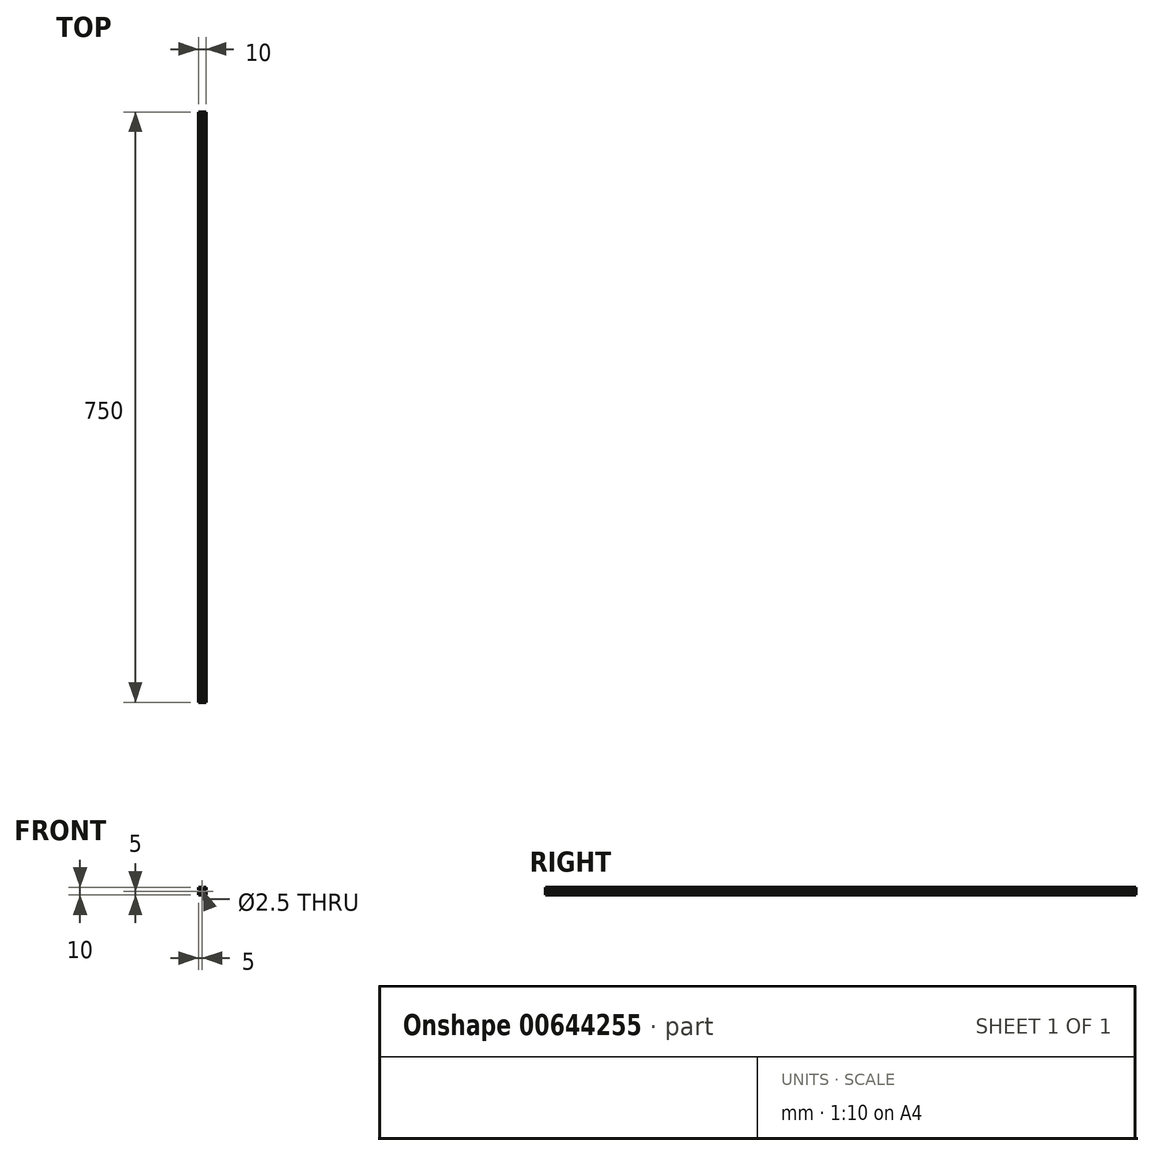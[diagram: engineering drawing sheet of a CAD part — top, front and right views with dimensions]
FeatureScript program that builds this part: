
annotation { "Feature Type Name" : "Feature", "Feature Type Description" : "" }
export const myFeature = defineFeature(function(context is Context, id is Id, definition is map)
    precondition{}
    {
        {
            var Q0;
            Q0=qCreatedBy(makeId("Front.planeOp"),FACE);
            var sketch = newSketch(context, id + "F0", { "sketchPlane" : qUnion([Q0])});
            skCircle(sketch, "E0", {"center": v(0, 0) * mm, "radius": 1.25 * mm});
            skLineSegment(sketch, "E1", {"start": v(1.5, 5) * mm, "end": v(5, 5) * mm});
            skLineSegment(sketch, "E2", {"start": v(5, 5) * mm, "end": v(5, 1.5) * mm});
            skLineSegment(sketch, "E3", {"start": v(5, -5) * mm, "end": v(1.5, -5) * mm});
            skLineSegment(sketch, "E4", {"start": v(-1.5, 5) * mm, "end": v(-5, 5) * mm});
            skLineSegment(sketch, "E5", {"start": v(-5, -5) * mm, "end": v(-5, -1.5) * mm});
            skLineSegment(sketch, "E6", {"start": v(5, -5) * mm, "end": v(5, -1.5) * mm});
            skLineSegment(sketch, "E7", {"start": v(5, -1.5) * mm, "end": v(4, -1.5) * mm});
            skLineSegment(sketch, "E8", {"start": v(1.5, -5) * mm, "end": v(1.5, -4) * mm});
            skLineSegment(sketch, "E9", {"start": v(0, 2) * mm, "end": v(-1, 2) * mm});
            skLineSegment(sketch, "E10", {"start": v(0, 2) * mm, "end": v(1, 2) * mm});
            skLineSegment(sketch, "E11", {"start": v(0, -2) * mm, "end": v(1, -2) * mm});
            skLineSegment(sketch, "E12", {"start": v(1.5, -4) * mm, "end": v(3, -4) * mm});
            skLineSegment(sketch, "E13", {"start": v(0, -2) * mm, "end": v(-1, -2) * mm});
            skLineSegment(sketch, "E14", {"start": v(4, -1.5) * mm, "end": v(4, -3) * mm});
            skLineSegment(sketch, "E15", {"start": v(0, 0) * mm, "end": v(1.25, 0) * mm});
            skLineSegment(sketch, "E16", {"start": v(-2, 0) * mm, "end": v(-2, 1) * mm});
            skLineSegment(sketch, "E17", {"start": v(-2, 0) * mm, "end": v(-2, -1) * mm});
            skLineSegment(sketch, "E18", {"start": v(2, 0) * mm, "end": v(2, 1) * mm});
            skLineSegment(sketch, "E19", {"start": v(2, 0) * mm, "end": v(2, -1) * mm});
            skLineSegment(sketch, "E20", {"start": v(1, -2) * mm, "end": v(3, -4) * mm});
            skLineSegment(sketch, "E21", {"start": v(2, -1) * mm, "end": v(4, -3) * mm});
            skLineSegment(sketch, "E22", {"start": v(5, 5) * mm, "end": v(1.5, 5) * mm});
            skLineSegment(sketch, "E23", {"start": v(1.5, 5) * mm, "end": v(1.5, 4) * mm});
            skLineSegment(sketch, "E24", {"start": v(5, 1.5) * mm, "end": v(4, 1.5) * mm});
            skLineSegment(sketch, "E25", {"start": v(4, 1.5) * mm, "end": v(4, 3) * mm});
            skLineSegment(sketch, "E26", {"start": v(1.5, 4) * mm, "end": v(3, 4) * mm});
            skLineSegment(sketch, "E27", {"start": v(1, 2) * mm, "end": v(3, 4) * mm});
            skLineSegment(sketch, "E28", {"start": v(2, 1) * mm, "end": v(4, 3) * mm});
            skLineSegment(sketch, "E29", {"start": v(-5, -5) * mm, "end": v(-1.5, -5) * mm});
            skLineSegment(sketch, "E30", {"start": v(-5, -1.5) * mm, "end": v(-4, -1.5) * mm});
            skLineSegment(sketch, "E31", {"start": v(-1.5, -5) * mm, "end": v(-1.5, -4) * mm});
            skLineSegment(sketch, "E32", {"start": v(-1.5, -4) * mm, "end": v(-3, -4) * mm});
            skLineSegment(sketch, "E33", {"start": v(-4, -1.5) * mm, "end": v(-4, -3) * mm});
            skLineSegment(sketch, "E34", {"start": v(-1, -2) * mm, "end": v(-3, -4) * mm});
            skLineSegment(sketch, "E35", {"start": v(-2, -1) * mm, "end": v(-4, -3) * mm});
            skLineSegment(sketch, "E36", {"start": v(-5, 5) * mm, "end": v(-1.5, 5) * mm});
            skLineSegment(sketch, "E37", {"start": v(-1.5, 5) * mm, "end": v(-1.5, 4) * mm});
            skLineSegment(sketch, "E38", {"start": v(-1.5, 4) * mm, "end": v(-3, 4) * mm});
            skLineSegment(sketch, "E39", {"start": v(-5, 5) * mm, "end": v(-5, 1.5) * mm});
            skLineSegment(sketch, "E40", {"start": v(-5, 1.5) * mm, "end": v(-4, 1.5) * mm});
            skLineSegment(sketch, "E41", {"start": v(-4, 1.5) * mm, "end": v(-4, 3) * mm});
            skLineSegment(sketch, "E42", {"start": v(-2, 1) * mm, "end": v(-4, 3) * mm});
            skLineSegment(sketch, "E43", {"start": v(-1, 2) * mm, "end": v(-3, 4) * mm});
            skLineSegment(sketch, "E44.trimOffspring", {"start": v(5, -1.5) * mm, "end": v(5, -5) * mm});
            skLineSegment(sketch, "E45.trimOffspring", {"start": v(-5, 1.5) * mm, "end": v(-5, 5) * mm});
            skLineSegment(sketch, "E46.trimOffspring", {"start": v(-1.5, -5) * mm, "end": v(-5, -5) * mm});
            skLineSegment(sketch, "E47.trimOffspring", {"start": v(0, 2) * mm, "end": v(0, 5) * mm});
            skSolve(sketch);
        }
        {
            var Q0;
            Q0 = qSketchRegion(id + "F0", true);
            extrude(context, id + "F1", {"entities" : qUnion([Q0]), "depth" : 750 * mm, "offsetDistance" : 25 * mm});
        }
    });
